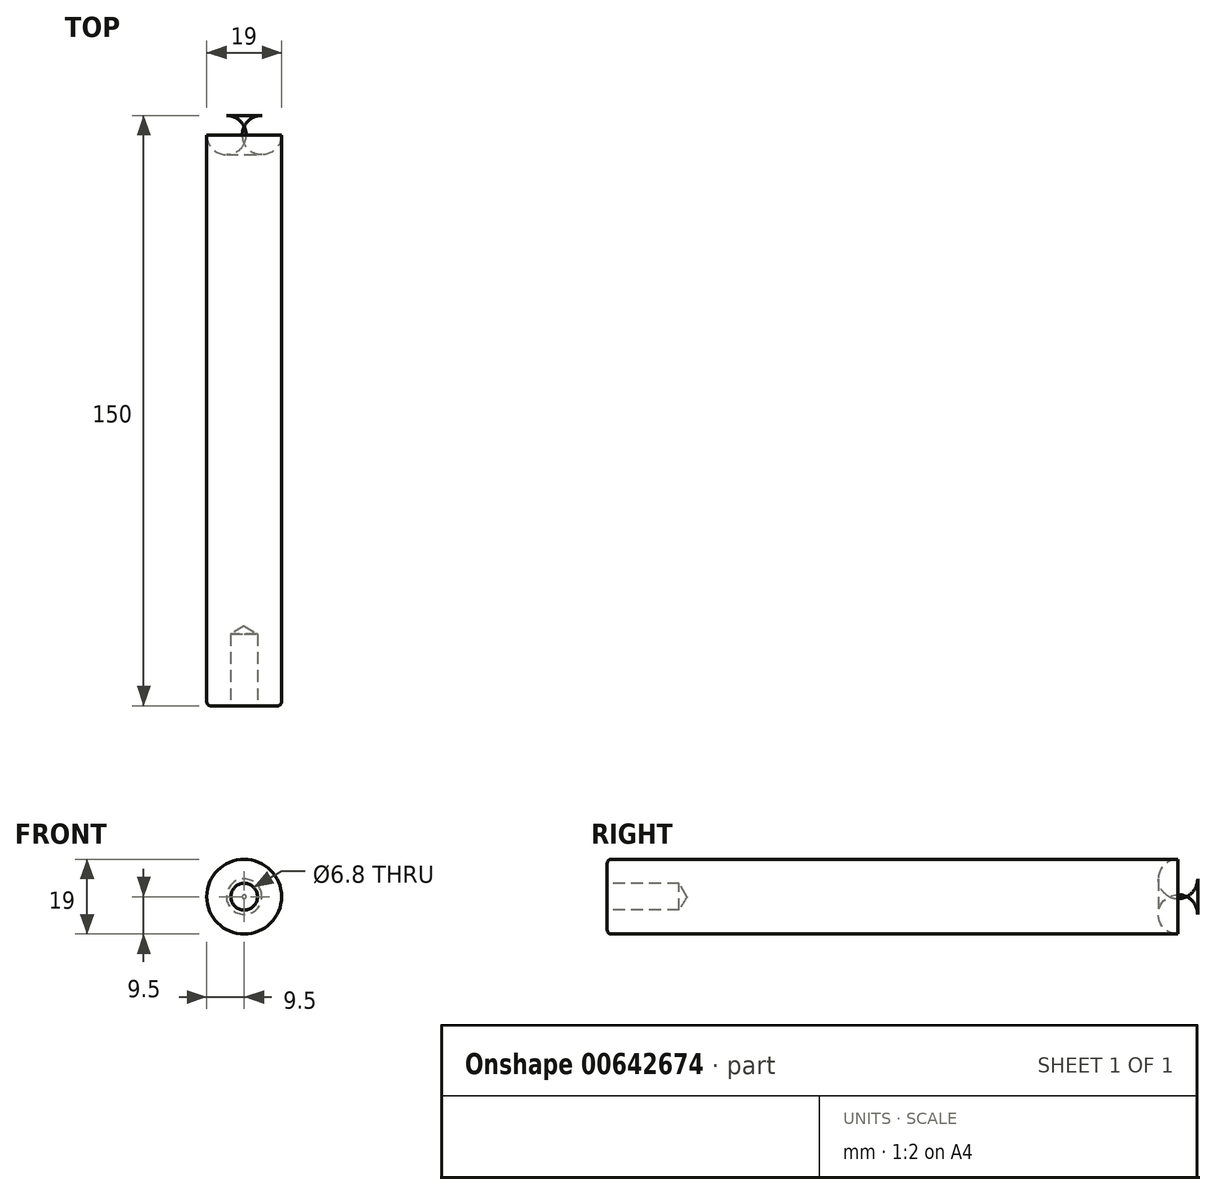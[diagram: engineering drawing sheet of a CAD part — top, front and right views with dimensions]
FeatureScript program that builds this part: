
annotation { "Feature Type Name" : "Feature", "Feature Type Description" : "" }
export const myFeature = defineFeature(function(context is Context, id is Id, definition is map)
    precondition{}
    {
        {
            var Q0;
            Q0=qCreatedBy(makeId("Front.planeOp"),FACE);
            var sketch = newSketch(context, id + "F0", { "sketchPlane" : qUnion([Q0])});
            skCircle(sketch, "E0", {"center": v(0, 0) * mm, "radius": 9.5 * mm});
            skSolve(sketch);
        }
        {
            var Q0;
            Q0=makeQuery(id+"F0.imprint","IMPRINT",FACE,{"disambiguationData":[TD([[makeQuery(id+"F0.imprint","IMPRINT",EDGE,{"derivedFrom":sQuery(id+"F0.wireOp",EDGE,"E0")}),1.0]])]});
            extrude(context, id + "F1", {"entities" : qUnion([Q0]), "depth" : 150 * mm, "offsetDistance" : 25 * mm});
        }
        {
            var Q0;
            Q0=makeQuery(id+"F1.opExtrude","CAP_FACE",FACE,{"disambiguationData":[OSD([sQuery(id+"F0.wireOp",EDGE,"E0")])],"isStart":false});
            var sketch = newSketch(context, id + "F2", { "sketchPlane" : qUnion([Q0])});
            skPoint(sketch, "E1", {"position": v(0, 0) * mm});
            skSolve(sketch);
        }
        {
            var Q0;
            Q0=sQuery(id+"F2.wireOp",VERTEX,"E1");
            var Q1;
            Q1=makeQuery(id+"F1.opExtrude","SWEPT_BODY",BODY,{"disambiguationData":[OSD([sQuery(id+"F0.wireOp",EDGE,"E0")])]});
            hole(context, id + "F3", {"style" : HoleStyle.SIMPLE, "endStyle" : HoleEndStyle.BLIND, "standardTappedOrClearance" : lookupTablePath({ "standard" : "ISO", "engagement" : "75%", "pitch" : "1.25 mm", "size" : "M8", "type" : "Tapped" }), "standardBlindInLast" : lookupTablePath({ "standard" : "ISO", "engagement" : "75%", "pitch" : "1.25 mm", "size" : "M8", "type" : "Tapped" }), "holeDiameter" : 6.8 * mm, "majorDiameter" : 8 * mm, "showTappedDepth" : true, "holeDepth" : 18.25 * mm, "isTappedThrough" : true, "tappedDepth" : 14.5 * mm, "tapClearance" : 3, "startFromSketch" : true, "locations" : qUnion([Q0]), "scope" : qUnion([Q1])});
        }
        {
            var Q0;
            Q0=makeQuery(id+"F1.opExtrude","CAP_EDGE",EDGE,{"disambiguationData":[OSD([sQuery(id+"F0.wireOp",EDGE,"E0")])],"isStart":false});
            fillet(context, id + "F4", {"entities" : qUnion([Q0]), "radius" : 1 * mm, "tangentPropagation" : true, "allowEdgeOverflow" : false});
        }
        {
            var Q0;
            Q0=makeQuery(id+"F1.opExtrude","SWEPT_FACE",FACE,{"disambiguationData":[OSD([sQuery(id+"F0.wireOp",EDGE,"E0")])]});
            var Q1;
            Q1=makeQuery(id+"F1.opExtrude","CAP_EDGE",EDGE,{"disambiguationData":[OSD([sQuery(id+"F0.wireOp",EDGE,"E0")])],"isStart":true});
            fillet(context, id + "F5", {"entities" : qUnion([Q0, Q1]), "radius" : 5 * mm, "tangentPropagation" : true, "allowEdgeOverflow" : false});
        }
    });
